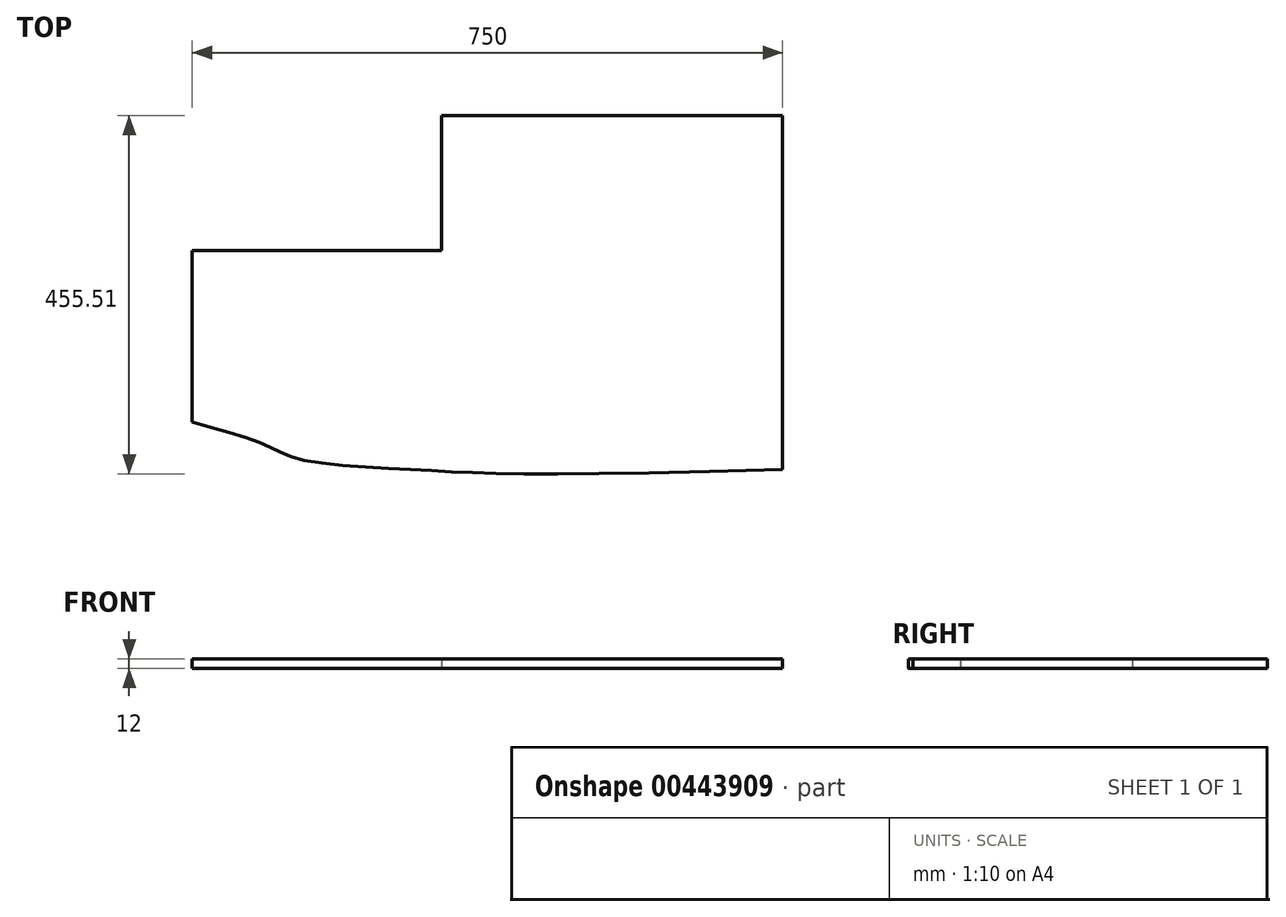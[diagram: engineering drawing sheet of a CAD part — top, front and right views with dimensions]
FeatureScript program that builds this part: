
annotation { "Feature Type Name" : "Feature", "Feature Type Description" : "" }
export const myFeature = defineFeature(function(context is Context, id is Id, definition is map)
    precondition{}
    {
        {
            var Q0;
            Q0=qCreatedBy(makeId("Top.planeOp"),FACE);
            var sketch = newSketch(context, id + "F0", { "sketchPlane" : qUnion([Q0])});
            skLineSegment(sketch, "E0", {"start": v(-750, 0) * mm, "end": v(-433.14, 0) * mm});
            skLineSegment(sketch, "E1", {"start": v(-433.14, 0) * mm, "end": v(-433.14, 171.51) * mm});
            skLineSegment(sketch, "E2", {"start": v(-433.14, 171.51) * mm, "end": v(0, 171.51) * mm});
            skLineSegment(sketch, "E3", {"start": v(0, 171.51) * mm, "end": v(0, -278.49) * mm});
            skFitSpline(sketch, "E4", {"points": [v(0, -278.49) * mm, v(-469.9, -278.49) * mm, v(-616.28, -264.53) * mm, v(-656.98, -247.1) * mm, v(-750, -218.02) * mm], "startDerivative": vector(-2328.35, -66.3) * mm, "endDerivative": vector(-565.9, 163.34) * mm});
            skLineSegment(sketch, "E5", {"start": v(-750, 0) * mm, "end": v(-750, -218.02) * mm});
            skSolve(sketch);
        }
        {
            var Q0;
            Q0=makeQuery(id+"F0.imprint","IMPRINT",FACE,{"disambiguationData":[TD([[makeQuery(id+"F0.imprint","IMPRINT",EDGE,{"derivedFrom":sQuery(id+"F0.wireOp",EDGE,"E0")}),-1.0]])]});
            extrude(context, id + "F1", {"entities" : qUnion([Q0]), "depth" : 12 * mm});
        }
        {
            var Q0;
            Q0=makeQuery(id+"F1.opExtrude","SWEPT_BODY",BODY,{"disambiguationData":[OSD([sQuery(id+"F0.wireOp",EDGE,"E0"),sQuery(id+"F0.wireOp",EDGE,"E1"),sQuery(id+"F0.wireOp",EDGE,"E2"),sQuery(id+"F0.wireOp",EDGE,"E3"),sQuery(id+"F0.wireOp",EDGE,"E4"),sQuery(id+"F0.wireOp",EDGE,"E5")])]});
            transform(context, id + "F2", {"entities" : qUnion([Q0]), "transformType" : TransformType.TRANSLATION_3D, "dx" : 0 * mm, "dy" : 0 * mm, "dz" : 0 * mm, "makeCopy" : true});
        }
    });
